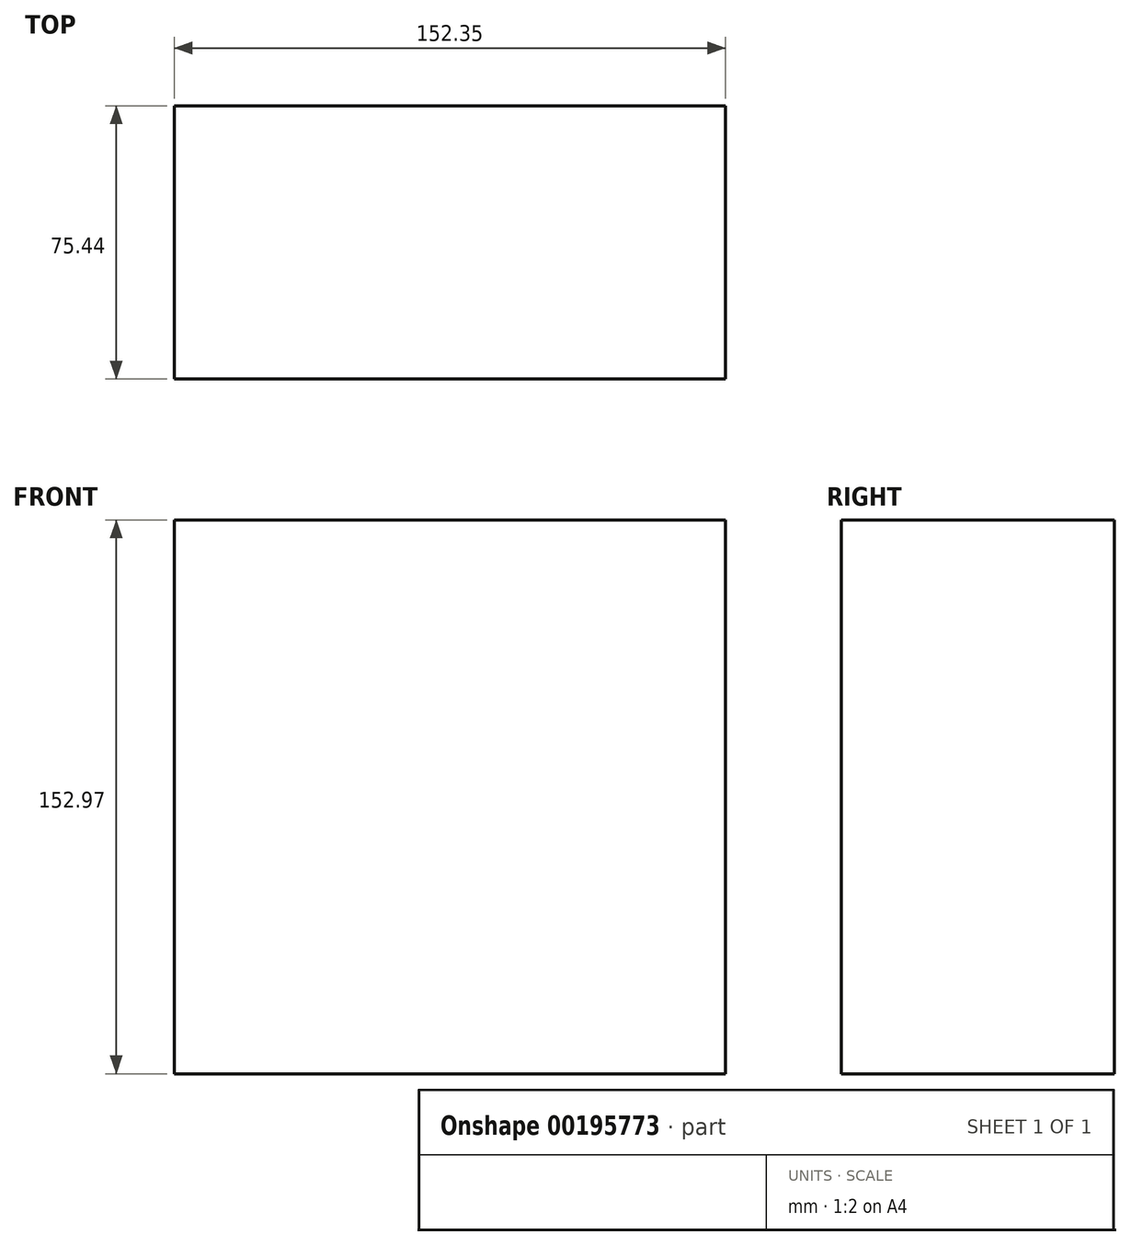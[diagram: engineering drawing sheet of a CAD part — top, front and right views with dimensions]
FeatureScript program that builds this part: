
annotation { "Feature Type Name" : "Feature", "Feature Type Description" : "" }
export const myFeature = defineFeature(function(context is Context, id is Id, definition is map)
    precondition{}
    {
        {
            var Q0;
            Q0=qCreatedBy(makeId("Front.planeOp"),FACE);
            var sketch = newSketch(context, id + "F0", { "sketchPlane" : qUnion([Q0])});
            skLineSegment(sketch, "E0.bottom", {"start": v(-76.33, 76.8) * mm, "end": v(76.02, 76.8) * mm});
            skLineSegment(sketch, "E0.top", {"start": v(-76.33, -76.18) * mm, "end": v(76.02, -76.18) * mm});
            skLineSegment(sketch, "E0.left", {"start": v(-76.33, 76.8) * mm, "end": v(-76.33, -76.18) * mm});
            skLineSegment(sketch, "E0.right", {"start": v(76.02, 76.8) * mm, "end": v(76.02, -76.18) * mm});
            skSolve(sketch);
        }
        {
            var Q0;
            Q0 = qSketchRegion(id + "F0", true);
            extrude(context, id + "F1", {"entities" : qUnion([Q0]), "depth" : 75.44 * mm});
        }
    });
